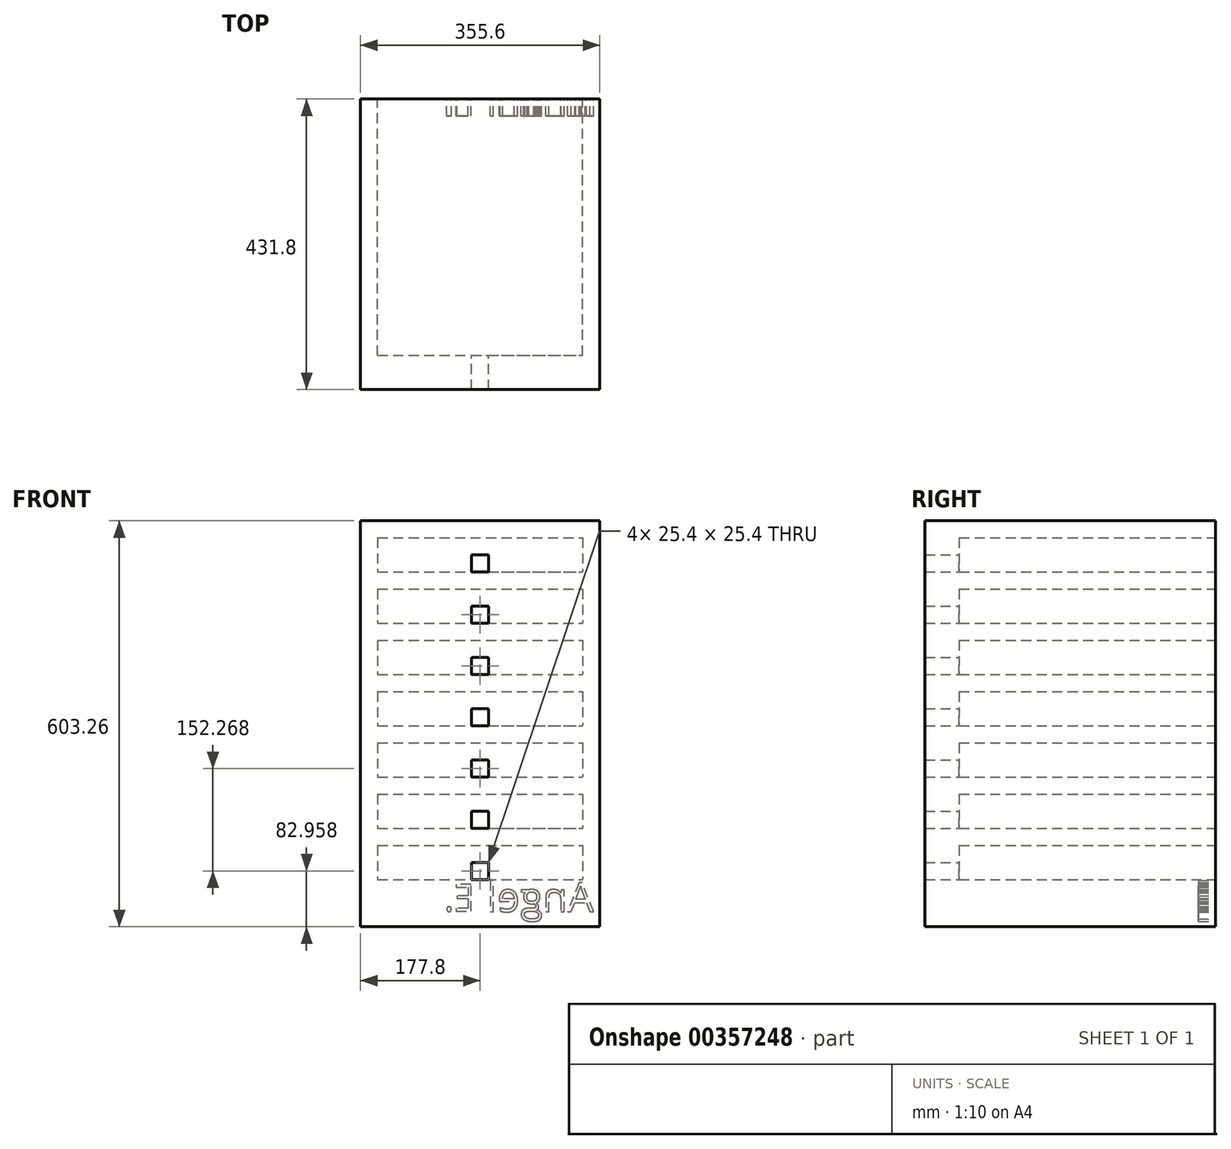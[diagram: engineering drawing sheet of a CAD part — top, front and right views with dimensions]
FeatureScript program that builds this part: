
annotation { "Feature Type Name" : "Feature", "Feature Type Description" : "" }
export const myFeature = defineFeature(function(context is Context, id is Id, definition is map)
    precondition{}
    {
        {
            var Q0;
            Q0=qCreatedBy(makeId("Front.planeOp"),FACE);
            var sketch = newSketch(context, id + "F0", { "sketchPlane" : qUnion([Q0])});
            skLineSegment(sketch, "E0", {"start": v(0, -301.63) * mm, "end": v(177.8, -301.63) * mm});
            skLineSegment(sketch, "E1", {"start": v(0, -301.63) * mm, "end": v(-177.8, -301.63) * mm});
            skLineSegment(sketch, "E2", {"start": v(0, 301.62) * mm, "end": v(177.8, 301.62) * mm});
            skLineSegment(sketch, "E3", {"start": v(0, 301.62) * mm, "end": v(-177.8, 301.62) * mm});
            skLineSegment(sketch, "E4", {"start": v(177.8, 301.63) * mm, "end": v(177.8, -301.63) * mm});
            skLineSegment(sketch, "E5", {"start": v(-177.8, 301.63) * mm, "end": v(-177.8, -301.63) * mm});
            skLineSegment(sketch, "E6", {"start": v(0, 301.62) * mm, "end": v(0, 0) * mm});
            skLineSegment(sketch, "E7", {"start": v(0, 0) * mm, "end": v(0, -301.63) * mm});
            skSolve(sketch);
        }
        {
            var Q0;
            Q0 = qSketchRegion(id + "F0", true);
            extrude(context, id + "F1", {"entities" : qUnion([Q0]), "depth" : 431.8 * mm});
        }
        {
            var Q0;
            Q0=makeQuery(id+"F1.opExtrude","CAP_FACE",FACE,{"disambiguationData":[OSD([sQuery(id+"F0.wireOp",EDGE,"E0"),sQuery(id+"F0.wireOp",EDGE,"E1"),sQuery(id+"F0.wireOp",EDGE,"E2"),sQuery(id+"F0.wireOp",EDGE,"E3"),sQuery(id+"F0.wireOp",EDGE,"E4"),sQuery(id+"F0.wireOp",EDGE,"E5")])],"isStart":true});
            var sketch = newSketch(context, id + "F2", { "sketchPlane" : qUnion([Q0])});
            skLineSegment(sketch, "E8", {"start": v(0, 301.62) * mm, "end": v(0, 276.22) * mm});
            skPoint(sketch, "E8.endSnap0", {"position": v(0, 301.62) * mm});
            skLineSegment(sketch, "E9", {"start": v(0, 276.22) * mm, "end": v(-152.4, 276.22) * mm});
            skLineSegment(sketch, "E10", {"start": v(0, 276.22) * mm, "end": v(0, 225.42) * mm});
            skLineSegment(sketch, "E11", {"start": v(0, 225.42) * mm, "end": v(0, 200.02) * mm});
            skLineSegment(sketch, "E12", {"start": v(0, 200.02) * mm, "end": v(0, 149.22) * mm});
            skLineSegment(sketch, "E13", {"start": v(0, 149.22) * mm, "end": v(0, 123.82) * mm});
            skLineSegment(sketch, "E14", {"start": v(0, 123.82) * mm, "end": v(0, 73.02) * mm});
            skLineSegment(sketch, "E15", {"start": v(0, 73.02) * mm, "end": v(0, 47.62) * mm});
            skLineSegment(sketch, "E16", {"start": v(0, 47.62) * mm, "end": v(0, -3.18) * mm});
            skLineSegment(sketch, "E17", {"start": v(0, -3.18) * mm, "end": v(0, -28.58) * mm});
            skLineSegment(sketch, "E18", {"start": v(0, -28.58) * mm, "end": v(0, -79.38) * mm});
            skLineSegment(sketch, "E19", {"start": v(0, -79.38) * mm, "end": v(0, -104.78) * mm});
            skLineSegment(sketch, "E20", {"start": v(0, -104.78) * mm, "end": v(0, -155.58) * mm});
            skLineSegment(sketch, "E21", {"start": v(0, -155.58) * mm, "end": v(0, -180.98) * mm});
            skLineSegment(sketch, "E22", {"start": v(0, -180.98) * mm, "end": v(0, -231.78) * mm});
            skLineSegment(sketch, "E23", {"start": v(0, -231.78) * mm, "end": v(0, -257.18) * mm});
            skLineSegment(sketch, "E24", {"start": v(0, 225.42) * mm, "end": v(-152.4, 225.42) * mm});
            skLineSegment(sketch, "E25", {"start": v(0, 200.02) * mm, "end": v(-152.4, 200.02) * mm});
            skLineSegment(sketch, "E26", {"start": v(0, 149.22) * mm, "end": v(-152.4, 149.22) * mm});
            skLineSegment(sketch, "E27", {"start": v(0, 123.82) * mm, "end": v(-152.4, 123.82) * mm});
            skLineSegment(sketch, "E28", {"start": v(0, 73.02) * mm, "end": v(-152.4, 73.02) * mm});
            skLineSegment(sketch, "E29", {"start": v(0, 47.62) * mm, "end": v(-152.4, 47.62) * mm});
            skLineSegment(sketch, "E30", {"start": v(0, -3.18) * mm, "end": v(-152.4, -3.18) * mm});
            skLineSegment(sketch, "E31", {"start": v(0, -28.58) * mm, "end": v(-152.4, -28.58) * mm});
            skLineSegment(sketch, "E32", {"start": v(0, -79.38) * mm, "end": v(-152.4, -79.38) * mm});
            skLineSegment(sketch, "E33", {"start": v(0, -104.78) * mm, "end": v(-152.4, -104.78) * mm});
            skLineSegment(sketch, "E34", {"start": v(0, -155.58) * mm, "end": v(-152.4, -155.58) * mm});
            skLineSegment(sketch, "E35", {"start": v(0, -180.98) * mm, "end": v(-152.4, -180.98) * mm});
            skLineSegment(sketch, "E36", {"start": v(0, -231.78) * mm, "end": v(-152.4, -231.78) * mm});
            skLineSegment(sketch, "E37", {"start": v(0, -257.18) * mm, "end": v(-152.4, -257.18) * mm});
            skLineSegment(sketch, "E38", {"start": v(-152.4, 276.22) * mm, "end": v(-152.4, 225.42) * mm});
            skLineSegment(sketch, "E39", {"start": v(-152.4, 200.02) * mm, "end": v(-152.4, 149.22) * mm});
            skLineSegment(sketch, "E40", {"start": v(-152.4, 123.82) * mm, "end": v(-152.4, 73.02) * mm});
            skLineSegment(sketch, "E41", {"start": v(-152.4, 47.62) * mm, "end": v(-152.4, -3.18) * mm});
            skLineSegment(sketch, "E42", {"start": v(-152.4, -28.58) * mm, "end": v(-152.4, -79.38) * mm});
            skLineSegment(sketch, "E43", {"start": v(-152.4, -104.78) * mm, "end": v(-152.4, -155.58) * mm});
            skLineSegment(sketch, "E44", {"start": v(-152.4, -180.98) * mm, "end": v(-152.4, -231.78) * mm});
            skLineSegment(sketch, "E45.MirrorCS", {"start": v(0, 276.22) * mm, "end": v(152.4, 276.22) * mm});
            skLineSegment(sketch, "E46.MirrorCS", {"start": v(0, 225.42) * mm, "end": v(152.4, 225.42) * mm});
            skLineSegment(sketch, "E47.MirrorCS", {"start": v(152.4, 276.22) * mm, "end": v(152.4, 225.42) * mm});
            skLineSegment(sketch, "E48.MirrorCS", {"start": v(0, 200.02) * mm, "end": v(152.4, 200.02) * mm});
            skLineSegment(sketch, "E49.MirrorCS", {"start": v(0, 149.22) * mm, "end": v(152.4, 149.22) * mm});
            skLineSegment(sketch, "E50.MirrorCS", {"start": v(0, 123.82) * mm, "end": v(152.4, 123.82) * mm});
            skLineSegment(sketch, "E51.MirrorCS", {"start": v(0, 73.02) * mm, "end": v(152.4, 73.02) * mm});
            skLineSegment(sketch, "E52.MirrorCS", {"start": v(0, 47.62) * mm, "end": v(152.4, 47.62) * mm});
            skLineSegment(sketch, "E53.MirrorCS", {"start": v(0, -3.18) * mm, "end": v(152.4, -3.18) * mm});
            skLineSegment(sketch, "E54.MirrorCS", {"start": v(0, -28.58) * mm, "end": v(152.4, -28.58) * mm});
            skLineSegment(sketch, "E55.MirrorCS", {"start": v(0, -79.38) * mm, "end": v(152.4, -79.38) * mm});
            skLineSegment(sketch, "E56.MirrorCS", {"start": v(0, -104.78) * mm, "end": v(152.4, -104.78) * mm});
            skLineSegment(sketch, "E57.MirrorCS", {"start": v(0, -155.58) * mm, "end": v(152.4, -155.58) * mm});
            skLineSegment(sketch, "E58.MirrorCS", {"start": v(0, -180.98) * mm, "end": v(152.4, -180.98) * mm});
            skLineSegment(sketch, "E59.MirrorCS", {"start": v(0, -231.78) * mm, "end": v(152.4, -231.78) * mm});
            skLineSegment(sketch, "E60.MirrorCS", {"start": v(0, -257.18) * mm, "end": v(152.4, -257.18) * mm});
            skLineSegment(sketch, "E61.MirrorCS", {"start": v(152.4, -180.98) * mm, "end": v(152.4, -231.78) * mm});
            skLineSegment(sketch, "E62.MirrorCS", {"start": v(152.4, -104.78) * mm, "end": v(152.4, -155.58) * mm});
            skLineSegment(sketch, "E63.MirrorCS", {"start": v(152.4, -28.58) * mm, "end": v(152.4, -79.38) * mm});
            skLineSegment(sketch, "E64.MirrorCS", {"start": v(152.4, 47.62) * mm, "end": v(152.4, -3.18) * mm});
            skLineSegment(sketch, "E65.MirrorCS", {"start": v(152.4, 123.82) * mm, "end": v(152.4, 73.02) * mm});
            skLineSegment(sketch, "E66.MirrorCS", {"start": v(152.4, 200.02) * mm, "end": v(152.4, 149.22) * mm});
            skSolve(sketch);
        }
        {
            var Q0;
            Q0=makeQuery(id+"F2.imprint","IMPRINT",FACE,{"disambiguationData":[TD([[makeQuery(id+"F2.imprint","IMPRINT",EDGE,{"derivedFrom":sQuery(id+"F2.wireOp",EDGE,"E14")}),-1.0]])]});
            var Q1;
            Q1=makeQuery(id+"F2.imprint","IMPRINT",FACE,{"disambiguationData":[TD([[makeQuery(id+"F2.imprint","IMPRINT",EDGE,{"derivedFrom":sQuery(id+"F2.wireOp",EDGE,"E16")}),-1.0]])]});
            var Q2;
            Q2=makeQuery(id+"F2.imprint","IMPRINT",FACE,{"disambiguationData":[TD([[makeQuery(id+"F2.imprint","IMPRINT",EDGE,{"derivedFrom":sQuery(id+"F2.wireOp",EDGE,"E18")}),-1.0]])]});
            var Q3;
            Q3=makeQuery(id+"F2.imprint","IMPRINT",FACE,{"disambiguationData":[TD([[makeQuery(id+"F2.imprint","IMPRINT",EDGE,{"derivedFrom":sQuery(id+"F2.wireOp",EDGE,"E20")}),-1.0]])]});
            var Q4;
            Q4=makeQuery(id+"F2.imprint","IMPRINT",FACE,{"disambiguationData":[TD([[makeQuery(id+"F2.imprint","IMPRINT",EDGE,{"derivedFrom":sQuery(id+"F2.wireOp",EDGE,"E22")}),-1.0]])]});
            var Q5;
            Q5=makeQuery(id+"F2.imprint","IMPRINT",FACE,{"disambiguationData":[TD([[makeQuery(id+"F2.imprint","IMPRINT",EDGE,{"derivedFrom":sQuery(id+"F2.wireOp",EDGE,"E12")}),-1.0]])]});
            var Q6;
            Q6=makeQuery(id+"F2.imprint","IMPRINT",FACE,{"disambiguationData":[TD([[makeQuery(id+"F2.imprint","IMPRINT",EDGE,{"derivedFrom":sQuery(id+"F2.wireOp",EDGE,"E9")}),1.0]])]});
            extrude(context, id + "F3", {"entities" : qUnion([Q0, Q1, Q2, Q3, Q4, Q5, Q6]), "operationType" : NewBodyOperationType.REMOVE, "oppositeDirection" : true, "depth" : 381 * mm});
        }
        {
            var Q0;
            Q0=makeQuery(id+"F2.imprint","IMPRINT",FACE,{"disambiguationData":[TD([[makeQuery(id+"F2.imprint","IMPRINT",EDGE,{"derivedFrom":sQuery(id+"F2.wireOp",EDGE,"E10")}),1.0]])]});
            var Q1;
            Q1=makeQuery(id+"F2.imprint","IMPRINT",FACE,{"disambiguationData":[TD([[makeQuery(id+"F2.imprint","IMPRINT",EDGE,{"derivedFrom":sQuery(id+"F2.wireOp",EDGE,"E12")}),1.0]])]});
            var Q2;
            Q2=makeQuery(id+"F2.imprint","IMPRINT",FACE,{"disambiguationData":[TD([[makeQuery(id+"F2.imprint","IMPRINT",EDGE,{"derivedFrom":sQuery(id+"F2.wireOp",EDGE,"E14")}),1.0]])]});
            var Q3;
            Q3=makeQuery(id+"F2.imprint","IMPRINT",FACE,{"disambiguationData":[TD([[makeQuery(id+"F2.imprint","IMPRINT",EDGE,{"derivedFrom":sQuery(id+"F2.wireOp",EDGE,"E16")}),1.0]])]});
            var Q4;
            Q4=makeQuery(id+"F2.imprint","IMPRINT",FACE,{"disambiguationData":[TD([[makeQuery(id+"F2.imprint","IMPRINT",EDGE,{"derivedFrom":sQuery(id+"F2.wireOp",EDGE,"E18")}),1.0]])]});
            var Q5;
            Q5=makeQuery(id+"F2.imprint","IMPRINT",FACE,{"disambiguationData":[TD([[makeQuery(id+"F2.imprint","IMPRINT",EDGE,{"derivedFrom":sQuery(id+"F2.wireOp",EDGE,"E20")}),1.0]])]});
            var Q6;
            Q6=makeQuery(id+"F2.imprint","IMPRINT",FACE,{"disambiguationData":[TD([[makeQuery(id+"F2.imprint","IMPRINT",EDGE,{"derivedFrom":sQuery(id+"F2.wireOp",EDGE,"E22")}),1.0]])]});
            extrude(context, id + "F4", {"entities" : qUnion([Q0, Q1, Q2, Q3, Q4, Q5, Q6]), "operationType" : NewBodyOperationType.REMOVE, "oppositeDirection" : true, "depth" : 381 * mm});
        }
        {
            var Q0;
            {var subQ0=sQuery(id+"F2.wireOp",EDGE,"E10");Q0=makeQuery(id+"F4.boolean.opBoolean","MERGE",FACE,{"derivedFrom":[makeQuery(id+"F3.boolean.opBoolean","COPY",FACE,{"derivedFrom":makeQuery(id+"F3.opExtrude","CAP_FACE",FACE,{"disambiguationData":[OSD([sQuery(id+"F2.wireOp",EDGE,"E9"),subQ0,sQuery(id+"F2.wireOp",EDGE,"E24"),sQuery(id+"F2.wireOp",EDGE,"E38")])],"isStart":false})}),makeQuery(id+"F4.opExtrude","CAP_FACE",FACE,{"disambiguationData":[OSD([subQ0,sQuery(id+"F2.wireOp",EDGE,"E45.MirrorCS"),sQuery(id+"F2.wireOp",EDGE,"E46.MirrorCS"),sQuery(id+"F2.wireOp",EDGE,"E47.MirrorCS")])],"isStart":false})]});}
            var sketch = newSketch(context, id + "F5", { "sketchPlane" : qUnion([Q0])});
            skLineSegment(sketch, "E67", {"start": v(0, 225.42) * mm, "end": v(12.7, 225.42) * mm});
            skLineSegment(sketch, "E68", {"start": v(0, 225.42) * mm, "end": v(-12.7, 225.42) * mm});
            skLineSegment(sketch, "E69", {"start": v(12.7, 225.42) * mm, "end": v(12.7, 250.82) * mm});
            skLineSegment(sketch, "E70", {"start": v(-12.7, 225.42) * mm, "end": v(-12.7, 250.82) * mm});
            skLineSegment(sketch, "E71", {"start": v(-12.7, 250.82) * mm, "end": v(12.7, 250.82) * mm});
            skLineSegment(sketch, "E72", {"start": v(0, 73.08) * mm, "end": v(12.7, 73.08) * mm});
            skLineSegment(sketch, "E73", {"start": v(0, 73.08) * mm, "end": v(-12.7, 73.08) * mm});
            skLineSegment(sketch, "E74", {"start": v(12.7, 73.08) * mm, "end": v(12.7, 98.48) * mm});
            skLineSegment(sketch, "E75", {"start": v(-12.7, 73.08) * mm, "end": v(-12.7, 98.48) * mm});
            skLineSegment(sketch, "E76", {"start": v(-12.7, 98.48) * mm, "end": v(12.7, 98.48) * mm});
            skLineSegment(sketch, "E77", {"start": v(0, 149.4) * mm, "end": v(12.7, 149.4) * mm});
            skLineSegment(sketch, "E78", {"start": v(12.7, 149.4) * mm, "end": v(12.7, 174.8) * mm});
            skLineSegment(sketch, "E79", {"start": v(0, 149.4) * mm, "end": v(-12.7, 149.4) * mm});
            skLineSegment(sketch, "E80", {"start": v(-12.7, 149.4) * mm, "end": v(-12.7, 174.8) * mm});
            skLineSegment(sketch, "E81", {"start": v(-12.7, 174.8) * mm, "end": v(12.7, 174.8) * mm});
            skLineSegment(sketch, "E82", {"start": v(0, -3.17) * mm, "end": v(12.7, -3.17) * mm});
            skLineSegment(sketch, "E83", {"start": v(12.7, -3.17) * mm, "end": v(12.7, 22.23) * mm});
            skLineSegment(sketch, "E84", {"start": v(0, -3.17) * mm, "end": v(-12.7, -3.17) * mm});
            skLineSegment(sketch, "E85", {"start": v(-12.7, -3.17) * mm, "end": v(-12.7, 22.23) * mm});
            skLineSegment(sketch, "E86", {"start": v(-12.7, 22.23) * mm, "end": v(12.7, 22.23) * mm});
            skLineSegment(sketch, "E87", {"start": v(0, -79.1) * mm, "end": v(12.7, -79.1) * mm});
            skLineSegment(sketch, "E88", {"start": v(12.7, -79.1) * mm, "end": v(12.7, -53.7) * mm});
            skLineSegment(sketch, "E89", {"start": v(0, -79.1) * mm, "end": v(-12.7, -79.1) * mm});
            skLineSegment(sketch, "E90", {"start": v(-12.7, -79.1) * mm, "end": v(-12.7, -53.7) * mm});
            skLineSegment(sketch, "E91", {"start": v(-12.7, -53.7) * mm, "end": v(12.7, -53.7) * mm});
            skLineSegment(sketch, "E92", {"start": v(0, -155.64) * mm, "end": v(12.7, -155.64) * mm});
            skLineSegment(sketch, "E93", {"start": v(12.7, -155.64) * mm, "end": v(12.7, -130.24) * mm});
            skLineSegment(sketch, "E94", {"start": v(0, -155.64) * mm, "end": v(-12.7, -155.64) * mm});
            skLineSegment(sketch, "E95", {"start": v(-12.7, -155.64) * mm, "end": v(-12.7, -130.24) * mm});
            skLineSegment(sketch, "E96", {"start": v(-12.7, -130.24) * mm, "end": v(12.7, -130.24) * mm});
            skLineSegment(sketch, "E97", {"start": v(0, -231.37) * mm, "end": v(12.7, -231.37) * mm});
            skLineSegment(sketch, "E98", {"start": v(12.7, -231.37) * mm, "end": v(12.7, -205.97) * mm});
            skLineSegment(sketch, "E99", {"start": v(0, -231.37) * mm, "end": v(-12.7, -231.37) * mm});
            skLineSegment(sketch, "E100", {"start": v(-12.7, -231.37) * mm, "end": v(-12.7, -205.97) * mm});
            skLineSegment(sketch, "E101", {"start": v(-12.7, -205.97) * mm, "end": v(12.7, -205.97) * mm});
            skSolve(sketch);
        }
        {
            var Q0;
            Q0=makeQuery(id+"F5.imprint","IMPRINT",FACE,{"disambiguationData":[TD([[makeQuery(id+"F5.imprint","IMPRINT",EDGE,{"derivedFrom":sQuery(id+"F5.wireOp",EDGE,"E67")}),-1.0]])]});
            extrude(context, id + "F6", {"entities" : qUnion([Q0]), "operationType" : NewBodyOperationType.REMOVE, "oppositeDirection" : true, "depth" : 256.54 * mm});
        }
        {
            var Q0;
            Q0=makeQuery(id+"F5.imprint","IMPRINT",FACE,{"disambiguationData":[TD([[makeQuery(id+"F5.imprint","IMPRINT",EDGE,{"derivedFrom":sQuery(id+"F5.wireOp",EDGE,"E72")}),1.0]])]});
            extrude(context, id + "F7", {"entities" : qUnion([Q0]), "operationType" : NewBodyOperationType.REMOVE, "oppositeDirection" : true, "depth" : 228.6 * mm});
        }
        {
            var Q0;
            Q0=makeQuery(id+"F5.imprint","IMPRINT",FACE,{"disambiguationData":[TD([[makeQuery(id+"F5.imprint","IMPRINT",EDGE,{"derivedFrom":sQuery(id+"F5.wireOp",EDGE,"E77")}),1.0]])]});
            extrude(context, id + "F8", {"entities" : qUnion([Q0]), "operationType" : NewBodyOperationType.REMOVE, "depth" : 482.6 * mm});
        }
        {
            var Q0;
            Q0=makeQuery(id+"F5.imprint","IMPRINT",FACE,{"disambiguationData":[TD([[makeQuery(id+"F5.imprint","IMPRINT",EDGE,{"derivedFrom":sQuery(id+"F5.wireOp",EDGE,"E77")}),1.0]])]});
            extrude(context, id + "F9", {"entities" : qUnion([Q0]), "operationType" : NewBodyOperationType.REMOVE, "oppositeDirection" : true, "depth" : 284.48 * mm});
        }
        {
            var Q0;
            Q0=makeQuery(id+"F5.imprint","IMPRINT",FACE,{"disambiguationData":[TD([[makeQuery(id+"F5.imprint","IMPRINT",EDGE,{"derivedFrom":sQuery(id+"F5.wireOp",EDGE,"E82")}),1.0]])]});
            extrude(context, id + "F10", {"entities" : qUnion([Q0]), "operationType" : NewBodyOperationType.REMOVE, "oppositeDirection" : true, "depth" : 259.84 * mm});
        }
        {
            var Q0;
            Q0=makeQuery(id+"F5.imprint","IMPRINT",FACE,{"disambiguationData":[TD([[makeQuery(id+"F5.imprint","IMPRINT",EDGE,{"derivedFrom":sQuery(id+"F5.wireOp",EDGE,"E87")}),1.0]])]});
            extrude(context, id + "F11", {"entities" : qUnion([Q0]), "operationType" : NewBodyOperationType.REMOVE, "oppositeDirection" : true, "depth" : 279.4 * mm});
        }
        {
            var Q0;
            Q0=makeQuery(id+"F5.imprint","IMPRINT",FACE,{"disambiguationData":[TD([[makeQuery(id+"F5.imprint","IMPRINT",EDGE,{"derivedFrom":sQuery(id+"F5.wireOp",EDGE,"E92")}),1.0]])]});
            extrude(context, id + "F12", {"entities" : qUnion([Q0]), "operationType" : NewBodyOperationType.REMOVE, "oppositeDirection" : true, "depth" : 254 * mm});
        }
        {
            var Q0;
            Q0=makeQuery(id+"F5.imprint","IMPRINT",FACE,{"disambiguationData":[TD([[makeQuery(id+"F5.imprint","IMPRINT",EDGE,{"derivedFrom":sQuery(id+"F5.wireOp",EDGE,"E97")}),1.0]])]});
            extrude(context, id + "F13", {"entities" : qUnion([Q0]), "operationType" : NewBodyOperationType.REMOVE, "oppositeDirection" : true, "depth" : 254 * mm});
        }
        {
            var Q0;
            Q0=makeQuery(id+"F1.opExtrude","CAP_FACE",FACE,{"disambiguationData":[OSD([sQuery(id+"F0.wireOp",EDGE,"E0"),sQuery(id+"F0.wireOp",EDGE,"E1"),sQuery(id+"F0.wireOp",EDGE,"E2"),sQuery(id+"F0.wireOp",EDGE,"E3"),sQuery(id+"F0.wireOp",EDGE,"E4"),sQuery(id+"F0.wireOp",EDGE,"E5")])],"isStart":true});
            var sketch = newSketch(context, id + "F14", { "sketchPlane" : qUnion([Q0])});
            skText(sketch, "E102", { "text": "Angel", "fontName": "OpenSans-Regular.ttf"});
            skLineSegment(sketch, "E103", {"start": v(-125.9, -279.35) * mm, "end": v(-120.87, -279.35) * mm});
            skLineSegment(sketch, "E104", {"start": v(-103.65, -279.35) * mm, "end": v(-98.63, -279.35) * mm});
            skText(sketch, "E105", { "text": "E.", "fontName": "OpenSans-Regular.ttf"});
            const initialGuessF14  = {"E102": [-0.16834, -0.27935, 1, 0, 0.04384], "E105": [0.00816, -0.27836, 1, 0, 0.0399]};
            skSetInitialGuess(sketch, initialGuessF14);
            skSolve(sketch);
        }
        {
            var Q0;
            Q0=makeQuery(id+"F14.imprint","IMPRINT",FACE,{"disambiguationData":[TD([[makeQuery(id+"F14.imprint","IMPRINT",EDGE,{"derivedFrom":sQuery(id+"F14.wireOp",EDGE,"E102.sketch_text.stroke-0")}),-1.0]])]});
            extrude(context, id + "F15", {"entities" : qUnion([Q0]), "operationType" : NewBodyOperationType.REMOVE, "oppositeDirection" : true, "depth" : 25.4 * mm});
        }
        {
            var Q0;
            {var subQ2=sQuery(id+"F14.wireOp",EDGE,"E102.sketch_text.stroke-13");Q0=makeQuery(id+"F14.imprint","IMPRINT",FACE,{"disambiguationData":[TD([[makeQuery(id+"F14.imprint","IMPRINT",EDGE,{"derivedFrom":subQ2}),-1.0]])]});}
            extrude(context, id + "F16", {"entities" : qUnion([Q0]), "operationType" : NewBodyOperationType.REMOVE, "oppositeDirection" : true, "depth" : 25.4 * mm});
        }
        {
            var Q0;
            Q0=makeQuery(id+"F14.imprint","IMPRINT",FACE,{"disambiguationData":[TD([[makeQuery(id+"F14.imprint","IMPRINT",EDGE,{"derivedFrom":sQuery(id+"F14.wireOp",EDGE,"E102.sketch_text.stroke-30")}),-1.0]])]});
            extrude(context, id + "F17", {"entities" : qUnion([Q0]), "operationType" : NewBodyOperationType.REMOVE, "oppositeDirection" : true, "depth" : 25.4 * mm});
        }
        {
            var Q0;
            Q0=makeQuery(id+"F14.imprint","IMPRINT",FACE,{"disambiguationData":[TD([[makeQuery(id+"F14.imprint","IMPRINT",EDGE,{"derivedFrom":sQuery(id+"F14.wireOp",EDGE,"E102.sketch_text.stroke-74")}),-1.0]])]});
            var Q1;
            Q1=makeQuery(id+"F14.imprint","IMPRINT",FACE,{"disambiguationData":[TD([[makeQuery(id+"F14.imprint","IMPRINT",EDGE,{"derivedFrom":sQuery(id+"F14.wireOp",EDGE,"E102.sketch_text.stroke-93")}),-1.0]])]});
            extrude(context, id + "F18", {"entities" : qUnion([Q0, Q1]), "operationType" : NewBodyOperationType.REMOVE, "oppositeDirection" : true, "depth" : 25.4 * mm});
        }
        {
            var Q0;
            Q0=makeQuery(id+"F14.imprint","IMPRINT",FACE,{"disambiguationData":[TD([[makeQuery(id+"F14.imprint","IMPRINT",EDGE,{"derivedFrom":sQuery(id+"F14.wireOp",EDGE,"E105.sketch_text.stroke-0")}),-1.0]])]});
            var Q1;
            Q1=makeQuery(id+"F14.imprint","IMPRINT",FACE,{"disambiguationData":[TD([[makeQuery(id+"F14.imprint","IMPRINT",EDGE,{"derivedFrom":sQuery(id+"F14.wireOp",EDGE,"E105.sketch_text.stroke-12")}),-1.0]])]});
            extrude(context, id + "F19", {"entities" : qUnion([Q0, Q1]), "operationType" : NewBodyOperationType.REMOVE, "oppositeDirection" : true, "depth" : 25.4 * mm});
        }
    });
